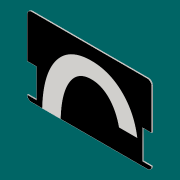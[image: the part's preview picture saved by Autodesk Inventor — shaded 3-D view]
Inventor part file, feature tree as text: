
AUTODESK INVENTOR PART (.ipt)
format: ipt  version: 2016 (Build 200138000, 138)  size: 219,136 bytes
history: native  units: mm
features: sketch x5, extrude x3, projected_geometry x3, other x2, fillet x1, mirror x1
ambient origin geometry x8: Origin, YZ Plane, XZ Plane, XY Plane, X Axis, Y Axis, Z Axis, Center Point
bodies: Solid1 (feature_tree)
feature tree (15):
  extrude  "Extrusion1"  Depth=53.98mm
  fillet  "Fillet1"  Radius=0.76mm
  extrude  "Extrusion2"  Depth=2.88mm
  extrude  "Extrusion3"  Depth=3.175mm
  mirror  "Mirror1"
  other  "Decal1"
  other  "Decal2"
  sketch  "Sketch1"  dims[d0=85.6mm d1=53.98mm d2=0.76mm]
  sketch  "Sketch2"  dims[d3=0.0mm d4=2.88mm]
  projected_geometry  "Projected Loop1"
  sketch  "Sketch3"  dims[d5=3.175mm d6=3.175mm]
  sketch  "Sketch4"  dims[d7=3.0mm]
  projected_geometry  "Projected Loop2"
  sketch  "Sketch5"  dims[d8=3.0mm d9=20.0mm d10=20.0mm d11=0.76mm d12=0.0mm d13=3.0mm d14=3.0mm d15=0.76mm d16=1.5mm d17=1.5mm d18=1.5mm d19=0.76mm d20=0.0mm]
  projected_geometry  "Projected Loop3"
